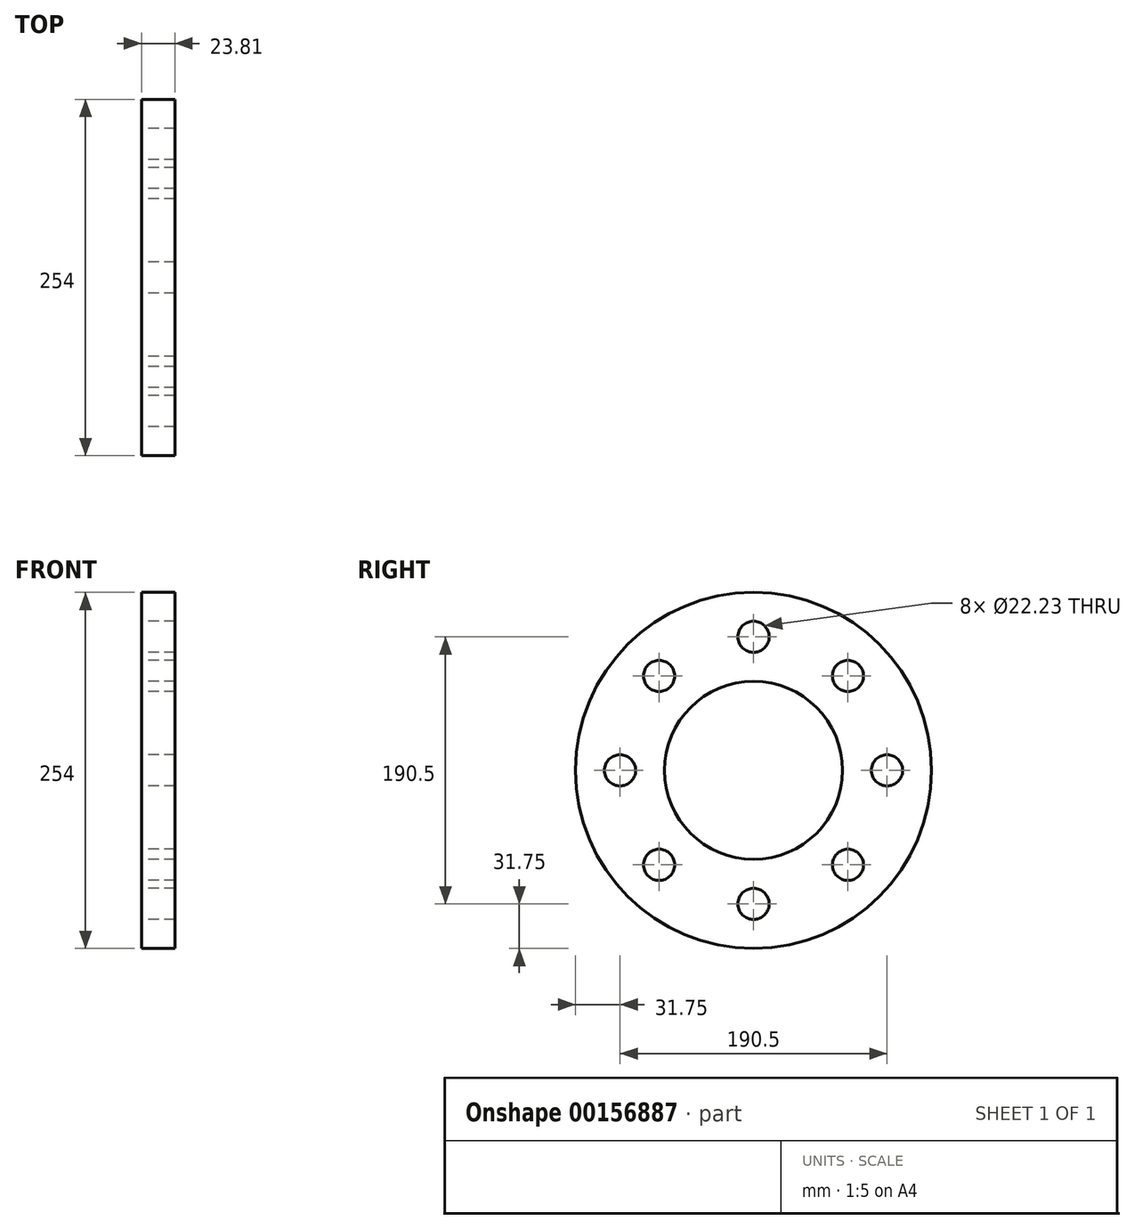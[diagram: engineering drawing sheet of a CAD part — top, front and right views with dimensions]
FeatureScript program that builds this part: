
annotation { "Feature Type Name" : "Feature", "Feature Type Description" : "" }
export const myFeature = defineFeature(function(context is Context, id is Id, definition is map)
    precondition{}
    {
        {
            var Q0;
            Q0=qCreatedBy(makeId("Right.planeOp"),FACE);
            var sketch = newSketch(context, id + "F0", { "sketchPlane" : qUnion([Q0])});
            skCircle(sketch, "E0", {"center": v(0, 0) * mm, "radius": 127 * mm});
            skCircle(sketch, "E1", {"center": v(0, 0) * mm, "radius": 63.5 * mm});
            skLineSegment(sketch, "E2", {"start": v(0, 172.37) * mm, "end": v(0, -171.6) * mm, "construction": true});
            skCircle(sketch, "E3", {"center": v(0, 95.25) * mm, "radius": 11.11 * mm});
            skCircle(sketch, "E4.1.0", {"center": v(-67.35, 67.35) * mm, "radius": 11.11 * mm});
            skCircle(sketch, "E4.2.0", {"center": v(-95.25, 0) * mm, "radius": 11.11 * mm});
            skCircle(sketch, "E4.3.0", {"center": v(-67.35, -67.35) * mm, "radius": 11.11 * mm});
            skCircle(sketch, "E4.4.0", {"center": v(0, -95.25) * mm, "radius": 11.11 * mm});
            skCircle(sketch, "E4.5.0", {"center": v(67.35, -67.35) * mm, "radius": 11.11 * mm});
            skCircle(sketch, "E4.6.0", {"center": v(95.25, 0) * mm, "radius": 11.11 * mm});
            skCircle(sketch, "E4.7.0", {"center": v(67.35, 67.35) * mm, "radius": 11.11 * mm});
            skSolve(sketch);
        }
        {
            var Q0;
            Q0=makeQuery(id+"F0.imprint","IMPRINT",FACE,{"disambiguationData":[TD([[makeQuery(id+"F0.imprint","IMPRINT",EDGE,{"derivedFrom":sQuery(id+"F0.wireOp",EDGE,"E0")}),1.0]])]});
            extrude(context, id + "F1", {"entities" : qUnion([Q0]), "depth" : 23.8 * mm});
        }
    });
